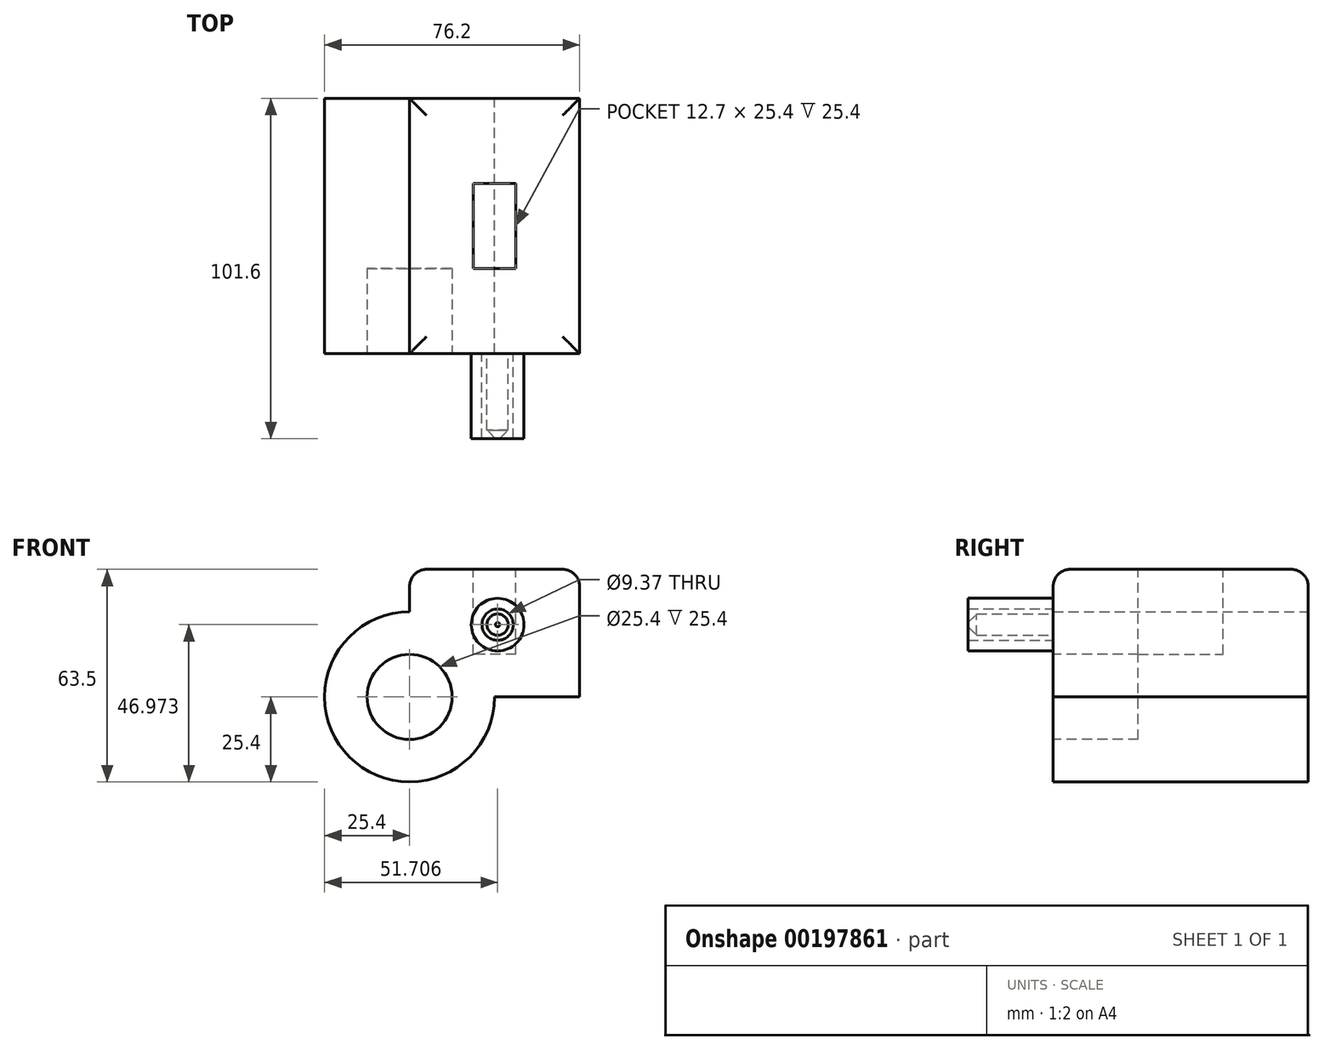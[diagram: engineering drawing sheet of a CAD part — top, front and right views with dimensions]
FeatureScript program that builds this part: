
annotation { "Feature Type Name" : "Feature", "Feature Type Description" : "" }
export const myFeature = defineFeature(function(context is Context, id is Id, definition is map)
    precondition{}
    {
        {
            var Q0;
            Q0=qCreatedBy(makeId("Front.planeOp"),FACE);
            var sketch = newSketch(context, id + "F0", { "sketchPlane" : qUnion([Q0])});
            skArc(sketch, "E0", {"start": v(0, 25.4) * mm, "mid": v(-17.96, -17.96) * mm, "end": v(25.4, 0) * mm});
            skLineSegment(sketch, "E1.bottom", {"start": v(25.4, 0) * mm, "end": v(50.8, 0) * mm});
            skLineSegment(sketch, "E1.top", {"start": v(0, 38.1) * mm, "end": v(50.8, 38.1) * mm});
            skLineSegment(sketch, "E1.left", {"start": v(0, 25.4) * mm, "end": v(0, 38.1) * mm});
            skLineSegment(sketch, "E1.right", {"start": v(50.8, 0) * mm, "end": v(50.8, 38.1) * mm});
            skSolve(sketch);
        }
        {
            var Q0;
            Q0 = qSketchRegion(id + "F0", true);
            extrude(context, id + "F1", {"entities" : qUnion([Q0]), "endBound" : BoundingType.SYMMETRIC, "depth" : 76.2 * mm});
        }
        {
            var Q0;
            Q0=makeQuery(id+"F1.opExtrude","SWEPT_FACE",FACE,{"disambiguationData":[OSD([sQuery(id+"F0.wireOp",EDGE,"E1.top")])]});
            var sketch = newSketch(context, id + "F2", { "sketchPlane" : qUnion([Q0])});
            skLineSegment(sketch, "E2.bottom", {"start": v(31.75, -12.7) * mm, "end": v(19.05, -12.7) * mm});
            skLineSegment(sketch, "E2.top", {"start": v(31.75, 12.7) * mm, "end": v(19.05, 12.7) * mm});
            skLineSegment(sketch, "E2.left", {"start": v(31.75, -12.7) * mm, "end": v(31.75, 12.7) * mm});
            skLineSegment(sketch, "E2.right", {"start": v(19.05, -12.7) * mm, "end": v(19.05, 12.7) * mm});
            skPoint(sketch, "E2.middle", {"position": v(25.4, 0) * mm});
            skPoint(sketch, "E2.middle.positionSnap0", {"position": v(25.4, 38.1) * mm});
            skPoint(sketch, "E2.centerSnap0", {"position": v(25.4, 38.1) * mm});
            skSolve(sketch);
        }
        {
            var Q0;
            Q0=makeQuery(id+"F2.imprint","IMPRINT",FACE,{"disambiguationData":[TD([[makeQuery(id+"F2.imprint","IMPRINT",EDGE,{"derivedFrom":sQuery(id+"F2.wireOp",EDGE,"E2.bottom")}),-1.0]])]});
            extrude(context, id + "F3", {"entities" : qUnion([Q0]), "operationType" : NewBodyOperationType.REMOVE, "oppositeDirection" : true, "depth" : 25.4 * mm});
        }
        {
            var Q0;
            Q0=makeQuery(id+"F1.opExtrude","CAP_EDGE",EDGE,{"disambiguationData":[OSD([sQuery(id+"F0.wireOp",EDGE,"E1.top")])],"isStart":false});
            var Q1;
            Q1=makeQuery(id+"F1.opExtrude","SWEPT_EDGE",EDGE,{"disambiguationData":[OSD([sQuery(id+"F0.wireOp",EDGE,"E1.top"),sQuery(id+"F0.wireOp",EDGE,"E1.right")])]});
            var Q2;
            Q2=makeQuery(id+"F1.opExtrude","CAP_EDGE",EDGE,{"disambiguationData":[OSD([sQuery(id+"F0.wireOp",EDGE,"E1.top")])],"isStart":true});
            var Q3;
            Q3=makeQuery(id+"F1.opExtrude","SWEPT_EDGE",EDGE,{"disambiguationData":[OSD([sQuery(id+"F0.wireOp",EDGE,"E1.top"),sQuery(id+"F0.wireOp",EDGE,"E1.left")])]});
            fillet(context, id + "F4", {"entities" : qUnion([Q0, Q1, Q2, Q3]), "radius" : 5.08 * mm, "tangentPropagation" : true, "allowEdgeOverflow" : false});
        }
        {
            var Q0;
            Q0=makeQuery(id+"F1.opExtrude","CAP_FACE",FACE,{"disambiguationData":[OSD([sQuery(id+"F0.wireOp",EDGE,"E0"),sQuery(id+"F0.wireOp",EDGE,"E1.bottom"),sQuery(id+"F0.wireOp",EDGE,"E1.top"),sQuery(id+"F0.wireOp",EDGE,"E1.left"),sQuery(id+"F0.wireOp",EDGE,"E1.right")])],"isStart":false});
            var sketch = newSketch(context, id + "F5", { "sketchPlane" : qUnion([Q0])});
            skCircle(sketch, "E3", {"center": v(0, 0) * mm, "radius": 12.7 * mm});
            skSolve(sketch);
        }
        {
            var Q0;
            Q0=makeQuery(id+"F5.imprint","IMPRINT",FACE,{"disambiguationData":[TD([[makeQuery(id+"F5.imprint","IMPRINT",EDGE,{"derivedFrom":sQuery(id+"F5.wireOp",EDGE,"E3")}),1.0]])]});
            extrude(context, id + "F6", {"entities" : qUnion([Q0]), "operationType" : NewBodyOperationType.REMOVE, "oppositeDirection" : true, "depth" : 25.4 * mm});
        }
        {
            var Q0;
            Q0=makeQuery(id+"F1.opExtrude","CAP_FACE",FACE,{"disambiguationData":[OSD([sQuery(id+"F0.wireOp",EDGE,"E0"),sQuery(id+"F0.wireOp",EDGE,"E1.bottom"),sQuery(id+"F0.wireOp",EDGE,"E1.top"),sQuery(id+"F0.wireOp",EDGE,"E1.left"),sQuery(id+"F0.wireOp",EDGE,"E1.right")])],"isStart":false});
            var sketch = newSketch(context, id + "F7", { "sketchPlane" : qUnion([Q0])});
            skCircle(sketch, "E4", {"center": v(26.3, 21.57) * mm, "radius": 3.18 * mm});
            skSolve(sketch);
        }
        {
            var Q0;
            Q0 = qSketchRegion(id + "F7", true);
            extrude(context, id + "F8", {"entities" : qUnion([Q0]), "operationType" : NewBodyOperationType.ADD, "depth" : 25.4 * mm});
        }
        {
            var Q0;
            Q0=makeQuery(id+"F8.opExtrude","CAP_EDGE",EDGE,{"disambiguationData":[OSD([sQuery(id+"F7.wireOp",EDGE,"E4")])],"isStart":false});
            chamfer(context, id + "F9", {"entities" : qUnion([Q0]), "width" : 2.54 * mm, "tangentPropagation" : true});
        }
        {
            var Q0;
            Q0=makeQuery(id+"F1.opExtrude","CAP_FACE",FACE,{"disambiguationData":[OSD([sQuery(id+"F0.wireOp",EDGE,"E0"),sQuery(id+"F0.wireOp",EDGE,"E1.bottom"),sQuery(id+"F0.wireOp",EDGE,"E1.top"),sQuery(id+"F0.wireOp",EDGE,"E1.left"),sQuery(id+"F0.wireOp",EDGE,"E1.right")])],"isStart":false});
            var sketch = newSketch(context, id + "F10", { "sketchPlane" : qUnion([Q0])});
            skCircle(sketch, "E5", {"center": v(26.3, 21.57) * mm, "radius": 7.87 * mm});
            skCircle(sketch, "E6", {"center": v(26.3, 21.57) * mm, "radius": 4.68 * mm});
            skSolve(sketch);
        }
        {
            var Q0;
            Q0=makeQuery(id+"F10.imprint","IMPRINT",FACE,{"disambiguationData":[TD([[makeQuery(id+"F10.imprint","IMPRINT",EDGE,{"derivedFrom":sQuery(id+"F10.wireOp",EDGE,"E5")}),1.0]])]});
            extrude(context, id + "F11", {"entities" : qUnion([Q0]), "depth" : 25.4 * mm});
        }
    });
